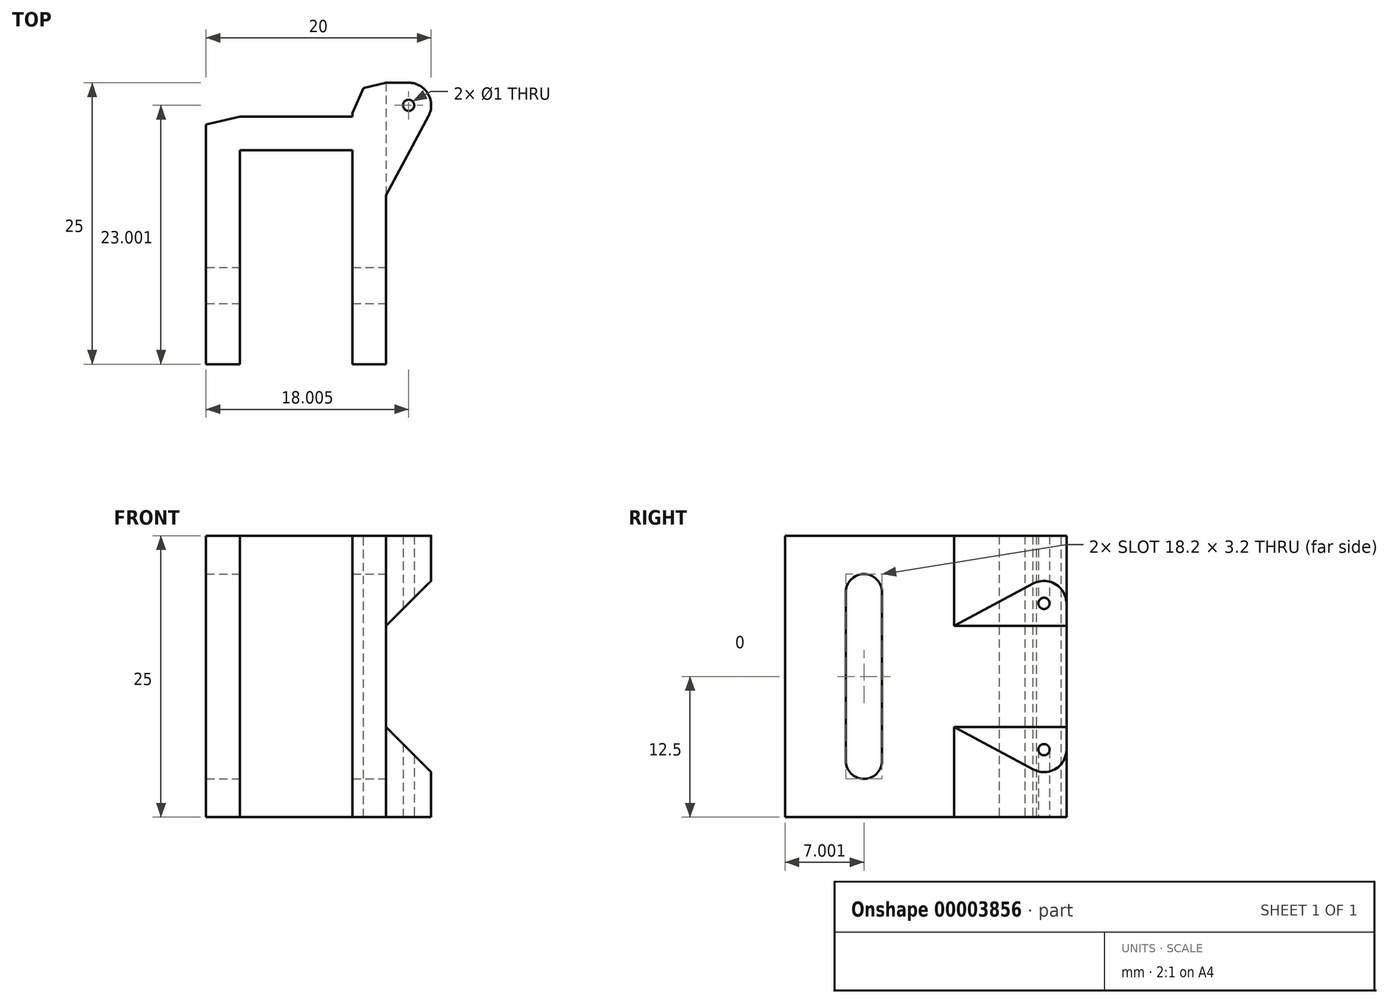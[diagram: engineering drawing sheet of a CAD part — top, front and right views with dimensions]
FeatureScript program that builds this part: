
annotation { "Feature Type Name" : "Feature", "Feature Type Description" : "" }
export const myFeature = defineFeature(function(context is Context, id is Id, definition is map)
    precondition{}
    {
        {
            var Q0;
            Q0=qCreatedBy(makeId("Top.planeOp"),FACE);
            var sketch = newSketch(context, id + "F0", { "sketchPlane" : qUnion([Q0])});
            skLineSegment(sketch, "E0", {"start": v(-92.53, 19.33) * mm, "end": v(-92.53, -5.67) * mm});
            skLineSegment(sketch, "E1", {"start": v(-92.53, -5.67) * mm, "end": v(-95.53, -5.67) * mm});
            skLineSegment(sketch, "E2", {"start": v(-95.53, -5.67) * mm, "end": v(-95.53, 13.33) * mm});
            skLineSegment(sketch, "E3", {"start": v(-95.53, 13.33) * mm, "end": v(-105.53, 13.33) * mm});
            skLineSegment(sketch, "E4", {"start": v(-105.53, 13.33) * mm, "end": v(-105.53, -5.67) * mm});
            skLineSegment(sketch, "E5", {"start": v(-105.53, -5.67) * mm, "end": v(-108.53, -5.67) * mm});
            skLineSegment(sketch, "E6", {"start": v(-108.53, -5.67) * mm, "end": v(-108.53, 15.64) * mm});
            skLineSegment(sketch, "E7", {"start": v(-105.53, 16.33) * mm, "end": v(-95.53, 16.33) * mm});
            skLineSegment(sketch, "E8", {"start": v(-95.53, 16.33) * mm, "end": v(-95.53, 18.64) * mm});
            skLineSegment(sketch, "E9", {"start": v(-92.53, 19.33) * mm, "end": v(-95.53, 18.64) * mm, "construction": true});
            skLineSegment(sketch, "E10", {"start": v(-105.53, 16.33) * mm, "end": v(-108.53, 15.64) * mm, "construction": true});
            skLineSegment(sketch, "E11", {"start": v(-108.53, 15.64) * mm, "end": v(-105.53, 16.33) * mm});
            skLineSegment(sketch, "E12", {"start": v(-92.53, 19.33) * mm, "end": v(-95.53, 18.64) * mm});
            skSolve(sketch);
        }
        {
            var Q0;
            Q0=makeQuery(id+"F0.imprint","IMPRINT",FACE,{"disambiguationData":[TD([[makeQuery(id+"F0.imprint","IMPRINT",EDGE,{"derivedFrom":sQuery(id+"F0.wireOp",EDGE,"E0")}),-1.0]])]});
            extrude(context, id + "F1", {"entities" : qUnion([Q0]), "depth" : 25 * mm});
        }
        {
            var Q0;
            Q0=makeQuery(id+"F1.opExtrude","CAP_FACE",FACE,{"disambiguationData":[OSD([sQuery(id+"F0.wireOp",EDGE,"E0"),sQuery(id+"F0.wireOp",EDGE,"E1"),sQuery(id+"F0.wireOp",EDGE,"E2"),sQuery(id+"F0.wireOp",EDGE,"E3"),sQuery(id+"F0.wireOp",EDGE,"E4"),sQuery(id+"F0.wireOp",EDGE,"E5"),sQuery(id+"F0.wireOp",EDGE,"E6"),sQuery(id+"F0.wireOp",EDGE,"E7"),sQuery(id+"F0.wireOp",EDGE,"E8"),sQuery(id+"F0.wireOp",EDGE,"E11"),sQuery(id+"F0.wireOp",EDGE,"E12")])],"isStart":true});
            var sketch = newSketch(context, id + "F2", { "sketchPlane" : qUnion([Q0])});
            skCircle(sketch, "E13", {"center": v(-90.53, -17.33) * mm, "radius": 0.5 * mm});
            skArc(sketch, "E14", {"start": v(-90.53, -19.33) * mm, "mid": v(-88.81, -18.36) * mm, "end": v(-88.76, -16.39) * mm});
            skLineSegment(sketch, "E15", {"start": v(-92.53, -19.33) * mm, "end": v(-90.53, -19.33) * mm});
            skLineSegment(sketch, "E16", {"start": v(-92.53, -9.33) * mm, "end": v(-88.76, -16.39) * mm});
            skLineSegment(sketch, "E17", {"start": v(-92.53, -19.33) * mm, "end": v(-92.53, -9.33) * mm});
            skSolve(sketch);
        }
        {
            var Q0;
            Q0=makeQuery(id+"F2.imprint","IMPRINT",FACE,{"disambiguationData":[TD([[makeQuery(id+"F2.imprint","IMPRINT",EDGE,{"derivedFrom":sQuery(id+"F2.wireOp",EDGE,"E13")}),-1.0]])]});
            extrude(context, id + "F3", {"entities" : qUnion([Q0]), "operationType" : NewBodyOperationType.ADD, "oppositeDirection" : true, "depth" : 25 * mm});
        }
        {
            var Q0;
            Q0=makeQuery(id+"F1.opExtrude","SWEPT_FACE",FACE,{"disambiguationData":[OSD([sQuery(id+"F0.wireOp",EDGE,"E1")])]});
            var sketch = newSketch(context, id + "F4", { "sketchPlane" : qUnion([Q0])});
            skLineSegment(sketch, "E18", {"start": v(-92.53, 17) * mm, "end": v(-82.19, 27.34) * mm});
            skLineSegment(sketch, "E19", {"start": v(-82.19, 27.34) * mm, "end": v(-82.19, -2.34) * mm});
            skLineSegment(sketch, "E20", {"start": v(-82.19, -2.34) * mm, "end": v(-92.53, 8) * mm});
            skLineSegment(sketch, "E21", {"start": v(-92.53, 8) * mm, "end": v(-92.53, 17) * mm});
            skSolve(sketch);
        }
        {
            var Q0;
            Q0=makeQuery(id+"F4.imprint","IMPRINT",FACE,{"disambiguationData":[TD([[makeQuery(id+"F4.imprint","IMPRINT",EDGE,{"derivedFrom":sQuery(id+"F4.wireOp",EDGE,"E18")}),-1.0]])]});
            extrude(context, id + "F5", {"entities" : qUnion([Q0]), "operationType" : NewBodyOperationType.REMOVE, "oppositeDirection" : true, "depth" : 30 * mm});
        }
        {
            var Q0;
            Q0=makeQuery(id+"F5.boolean.opBoolean","MERGE",FACE,{"derivedFrom":[makeQuery(id+"F1.opExtrude","SWEPT_FACE",FACE,{"disambiguationData":[OSD([sQuery(id+"F0.wireOp",EDGE,"E0")])]}),makeQuery(id+"F5.opExtrude","SWEPT_FACE",FACE,{"disambiguationData":[OSD([sQuery(id+"F4.wireOp",EDGE,"E21")])]})]});
            var sketch = newSketch(context, id + "F6", { "sketchPlane" : qUnion([Q0])});
            skArc(sketch, "E22", {"start": v(2.93, 20) * mm, "mid": v(1.33, 21.6) * mm, "end": v(-0.27, 20) * mm});
            skArc(sketch, "E23", {"start": v(-0.27, 5) * mm, "mid": v(1.33, 3.4) * mm, "end": v(2.93, 5) * mm});
            skLineSegment(sketch, "E24.right", {"start": v(2.93, 20) * mm, "end": v(2.93, 5) * mm});
            skLineSegment(sketch, "E25.right", {"start": v(-0.27, 5) * mm, "end": v(-0.27, 20) * mm});
            skSolve(sketch);
        }
        {
            var Q0;
            Q0=makeQuery(id+"F6.imprint","IMPRINT",FACE,{"disambiguationData":[TD([[makeQuery(id+"F6.imprint","IMPRINT",EDGE,{"derivedFrom":sQuery(id+"F6.wireOp",EDGE,"E22")}),1.0]])]});
            extrude(context, id + "F7", {"entities" : qUnion([Q0]), "operationType" : NewBodyOperationType.REMOVE, "oppositeDirection" : true, "depth" : 25 * mm});
        }
        {
            var Q0;
            Q0=makeQuery(id+"F1.opExtrude","SWEPT_EDGE",EDGE,{"disambiguationData":[OSD([sQuery(id+"F0.wireOp",EDGE,"E8"),sQuery(id+"F0.wireOp",EDGE,"E12")])]});
            chamfer(context, id + "F8", {"entities" : qUnion([Q0]), "chamferType" : ChamferType.TWO_OFFSETS, "width1" : 2 * mm, "oppositeDirection" : false, "width2" : 1 * mm, "tangentPropagation" : true});
        }
    });
